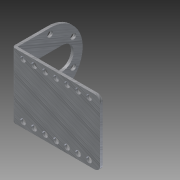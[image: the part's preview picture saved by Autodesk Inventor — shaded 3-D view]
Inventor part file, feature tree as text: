
AUTODESK INVENTOR PART (.ipt)
format: ipt  version: 2012 (Build 160160000, 160)  size: 196,096 bytes
history: native  units: mm
features: extrude x3, sketch x3, projected_geometry x1
ambient origin geometry x8: Origin, YZ Plane, XZ Plane, XY Plane, X Axis, Y Axis, Z Axis, Center Point
bodies: Solid1 (feature_tree)
feature tree (7):
  extrude  "Extrusion1"  Depth=37.59mm
  extrude  "Extrusion2"  Depth=37.59mm TaperAngle=0.0deg
  extrude  "Extrusion3"  Depth=6.35mm
  sketch  "Sketch1"  dims[d0=49.21mm d1=37.59mm]
  sketch  "Sketch3"  dims[d2=1.59mm d3=37.59mm d4=0.0mm]
  projected_geometry  "Projected Loop1"
  sketch  "Sketch4"  dims[d12=6.35mm d13=6.35mm d14=6.35mm d15=6.35mm d16=6.35mm d17=6.35mm d18=6.35mm d19=3.18mm d20=15.62mm d21=10.0mm d22=37.59mm d23=0.0mm d24=13.21mm d25=14.02mm d26=12.19mm d27=11.785mm d28=15.5mm d29=15.5mm d30=15.5mm d31=15.5mm d32=15.5mm d33=15.5mm d34=3.25mm d35=60.0mm d37=360.0deg d39=10.0mm d40=0.0mm]
